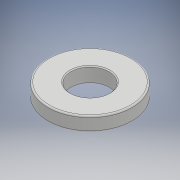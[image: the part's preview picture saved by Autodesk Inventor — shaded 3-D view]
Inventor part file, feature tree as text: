
AUTODESK INVENTOR PART (.ipt)
format: ipt  version: 2018.2 (Build 222227000, 227)  size: 122,880 bytes
history: native  units: mm
features: extrude x1, fillet x1, chamfer x1, sketch x1
ambient origin geometry x8: Origin, YZ Plane, XZ Plane, XY Plane, X Axis, Y Axis, Z Axis, Center Point
bodies: Solid1 (feature_tree)
feature tree (4):
  extrude  "Extrusion1"  Depth=0.4mm
  fillet  "Fillet1"  Radius=2.0mm
  chamfer  "Chamfer1"  Distance=2.0mm
  sketch  "Sketch1"  dims[d0=10.1mm d1=6.0mm d2=2.0mm d3=2.0mm d4=3.8mm d5=0.0mm d6=0.4mm d7=0.25mm d8=2.0mm d9=45.0deg]
